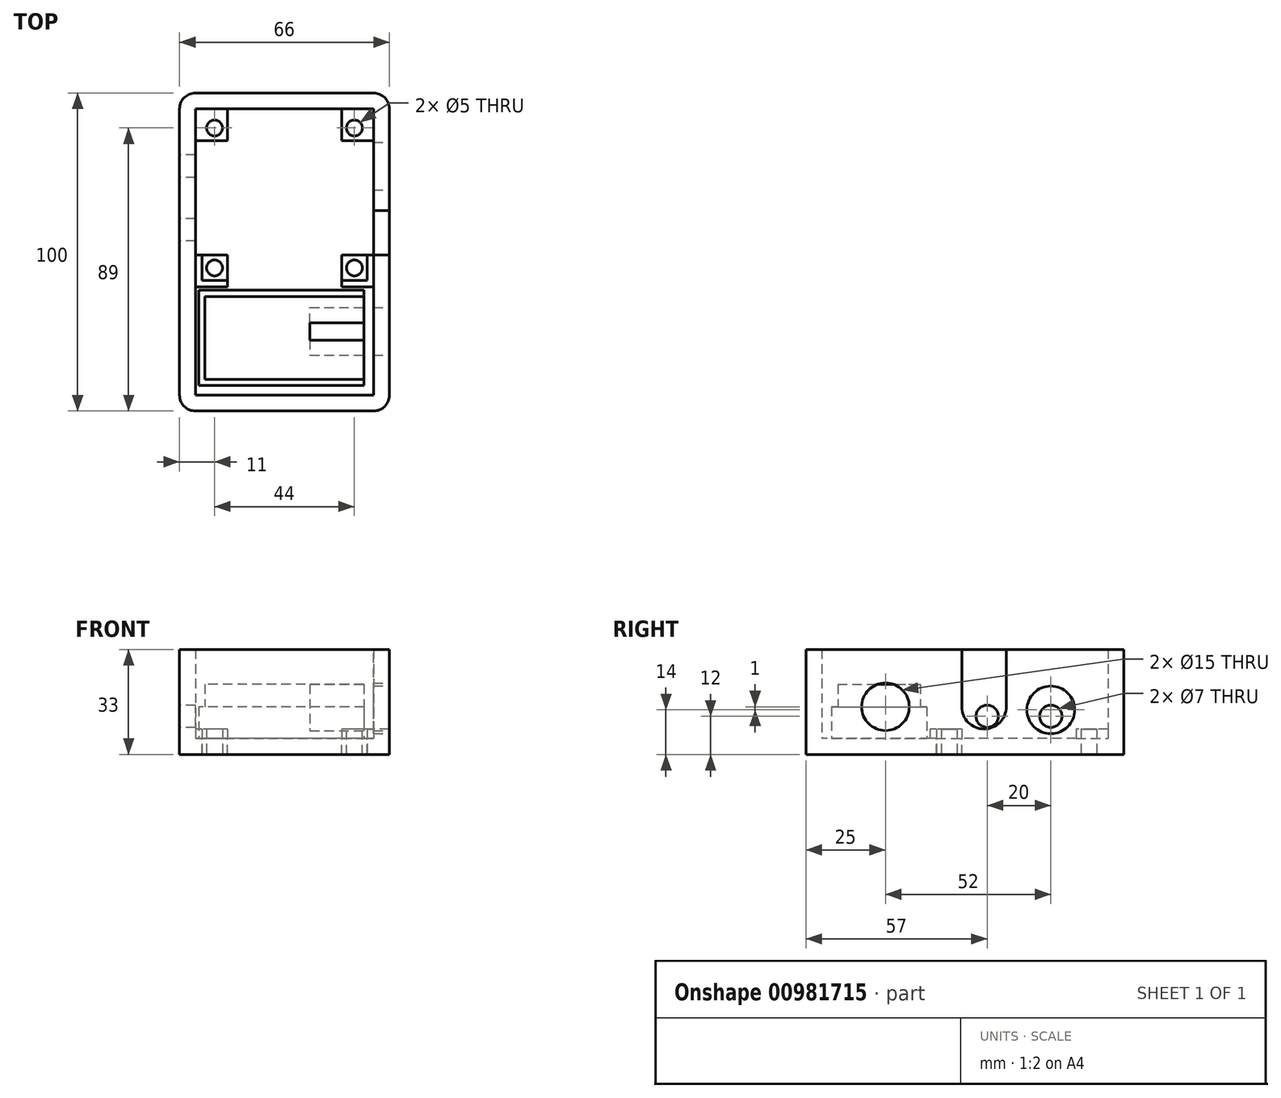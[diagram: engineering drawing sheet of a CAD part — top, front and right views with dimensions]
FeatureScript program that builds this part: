
annotation { "Feature Type Name" : "Feature", "Feature Type Description" : "" }
export const myFeature = defineFeature(function(context is Context, id is Id, definition is map)
    precondition{}
    {
        {
            var Q0;
            Q0=qCreatedBy(makeId("Top.planeOp"),FACE);
            var sketch = newSketch(context, id + "F0", { "sketchPlane" : qUnion([Q0])});
            skLineSegment(sketch, "E0.bottom", {"start": v(26, 26) * mm, "end": v(-26, 26) * mm});
            skLineSegment(sketch, "E0.top", {"start": v(26, -26) * mm, "end": v(-26, -26) * mm});
            skLineSegment(sketch, "E0.left", {"start": v(26, 26) * mm, "end": v(26, -26) * mm});
            skLineSegment(sketch, "E0.right", {"start": v(-26, 26) * mm, "end": v(-26, -26) * mm});
            skPoint(sketch, "E0.middle", {"position": v(0, 0) * mm});
            skCircle(sketch, "E1", {"center": v(-22, 22) * mm, "radius": 2.5 * mm});
            skCircle(sketch, "E2", {"center": v(22, 22) * mm, "radius": 2.5 * mm});
            skLineSegment(sketch, "E3", {"start": v(-22, 22) * mm, "end": v(-26, 22) * mm, "construction": true});
            skLineSegment(sketch, "E4", {"start": v(22, 22) * mm, "end": v(26, 22) * mm, "construction": true});
            skLineSegment(sketch, "E5", {"start": v(-22, 22) * mm, "end": v(-22, 26) * mm, "construction": true});
            skLineSegment(sketch, "E6", {"start": v(22, 22) * mm, "end": v(22, 26) * mm, "construction": true});
            skLineSegment(sketch, "E7", {"start": v(-26, 0) * mm, "end": v(26, 0) * mm, "construction": true});
            skCircle(sketch, "E8.MirrorC", {"center": v(-22, -22) * mm, "radius": 2.5 * mm});
            skCircle(sketch, "E9.MirrorC", {"center": v(22, -22) * mm, "radius": 2.5 * mm});
            skLineSegment(sketch, "E10.bottom", {"start": v(26, -4) * mm, "end": v(13, -4) * mm});
            skLineSegment(sketch, "E10.top", {"start": v(26, -18) * mm, "end": v(13, -18) * mm});
            skLineSegment(sketch, "E10.left", {"start": v(26, -4) * mm, "end": v(26, -18) * mm});
            skLineSegment(sketch, "E10.right", {"start": v(13, -4) * mm, "end": v(13, -18) * mm});
            skLineSegment(sketch, "E11.bottom", {"start": v(26, 15) * mm, "end": v(12, 15) * mm});
            skLineSegment(sketch, "E11.top", {"start": v(26, 5) * mm, "end": v(12, 5) * mm});
            skLineSegment(sketch, "E11.left", {"start": v(26, 15) * mm, "end": v(26, 5) * mm});
            skLineSegment(sketch, "E11.right", {"start": v(12, 15) * mm, "end": v(12, 5) * mm});
            skLineSegment(sketch, "E12.bottom", {"start": v(-26, 16) * mm, "end": v(-11, 16) * mm});
            skLineSegment(sketch, "E12.top", {"start": v(-26, 4) * mm, "end": v(-11, 4) * mm});
            skLineSegment(sketch, "E12.left", {"start": v(-26, 16) * mm, "end": v(-26, 4) * mm});
            skLineSegment(sketch, "E12.right", {"start": v(-11, 16) * mm, "end": v(-11, 4) * mm});
            skLineSegment(sketch, "E13.bottom", {"start": v(-26, -4) * mm, "end": v(-11, -4) * mm});
            skLineSegment(sketch, "E13.top", {"start": v(-26, -16) * mm, "end": v(-11, -16) * mm});
            skLineSegment(sketch, "E13.left", {"start": v(-26, -4) * mm, "end": v(-26, -16) * mm});
            skLineSegment(sketch, "E13.right", {"start": v(-11, -4) * mm, "end": v(-11, -16) * mm});
            skLineSegment(sketch, "E14.0", {"start": v(28, 28) * mm, "end": v(-28, 28) * mm});
            skLineSegment(sketch, "E14.1", {"start": v(28, 28) * mm, "end": v(28, -28) * mm});
            skLineSegment(sketch, "E14.2", {"start": v(28, -28) * mm, "end": v(-28, -28) * mm});
            skLineSegment(sketch, "E14.3", {"start": v(-28, 28) * mm, "end": v(-28, -28) * mm});
            skLineSegment(sketch, "E15.0", {"start": v(33, 33) * mm, "end": v(-33, 33) * mm});
            skLineSegment(sketch, "E15.1", {"start": v(33, 33) * mm, "end": v(33, -67) * mm});
            skLineSegment(sketch, "E15.3", {"start": v(-33, 33) * mm, "end": v(-33, -67) * mm});
            skLineSegment(sketch, "E16.bottom", {"start": v(1, 9) * mm, "end": v(-9, 9) * mm});
            skLineSegment(sketch, "E16.top", {"start": v(1, -1) * mm, "end": v(-9, -1) * mm});
            skLineSegment(sketch, "E16.left", {"start": v(1, 9) * mm, "end": v(1, -1) * mm});
            skLineSegment(sketch, "E16.right", {"start": v(-9, 9) * mm, "end": v(-9, -1) * mm});
            skPoint(sketch, "E16.middle", {"position": v(-4, 4) * mm});
            skCircle(sketch, "E17", {"center": v(-4, 4) * mm, "radius": 5 * mm});
            skLineSegment(sketch, "E18.bottom", {"start": v(26, 26) * mm, "end": v(18, 26) * mm});
            skLineSegment(sketch, "E18.top", {"start": v(26, 18) * mm, "end": v(18, 18) * mm});
            skLineSegment(sketch, "E18.left", {"start": v(26, 26) * mm, "end": v(26, 18) * mm});
            skLineSegment(sketch, "E18.right", {"start": v(18, 26) * mm, "end": v(18, 18) * mm});
            skLineSegment(sketch, "E19.bottom", {"start": v(-26, 26) * mm, "end": v(-18, 26) * mm});
            skLineSegment(sketch, "E19.top", {"start": v(-26, 18) * mm, "end": v(-18, 18) * mm});
            skLineSegment(sketch, "E19.left", {"start": v(-26, 26) * mm, "end": v(-26, 18) * mm});
            skLineSegment(sketch, "E19.right", {"start": v(-18, 26) * mm, "end": v(-18, 18) * mm});
            skLineSegment(sketch, "E20.bottom", {"start": v(-26, -26) * mm, "end": v(-18, -26) * mm});
            skLineSegment(sketch, "E20.top", {"start": v(-26, -18) * mm, "end": v(-18, -18) * mm});
            skLineSegment(sketch, "E20.left", {"start": v(-26, -26) * mm, "end": v(-26, -18) * mm});
            skLineSegment(sketch, "E20.right", {"start": v(-18, -26) * mm, "end": v(-18, -18) * mm});
            skLineSegment(sketch, "E21.bottom", {"start": v(26, -26) * mm, "end": v(18, -26) * mm});
            skLineSegment(sketch, "E21.top", {"start": v(26, -18) * mm, "end": v(18, -18) * mm});
            skLineSegment(sketch, "E21.left", {"start": v(26, -26) * mm, "end": v(26, -18) * mm});
            skLineSegment(sketch, "E21.right", {"start": v(18, -26) * mm, "end": v(18, -18) * mm});
            skLineSegment(sketch, "E22", {"start": v(-18, 26) * mm, "end": v(-18, 28) * mm});
            skLineSegment(sketch, "E23", {"start": v(-26, 18) * mm, "end": v(-28, 18) * mm});
            skLineSegment(sketch, "E24", {"start": v(-18, -26) * mm, "end": v(-18, -28) * mm});
            skLineSegment(sketch, "E25", {"start": v(-26, -18) * mm, "end": v(-28, -18) * mm});
            skLineSegment(sketch, "E26", {"start": v(26, -18) * mm, "end": v(28, -18) * mm});
            skLineSegment(sketch, "E27", {"start": v(18, -26) * mm, "end": v(18, -28) * mm});
            skLineSegment(sketch, "E28", {"start": v(26, 18) * mm, "end": v(28, 18) * mm});
            skLineSegment(sketch, "E29", {"start": v(18, 26) * mm, "end": v(18, 28) * mm});
            skLineSegment(sketch, "E30.bottom", {"start": v(25, -57) * mm, "end": v(-25, -57) * mm});
            skLineSegment(sketch, "E30.top", {"start": v(25, -31) * mm, "end": v(-25, -31) * mm});
            skLineSegment(sketch, "E30.left", {"start": v(25, -57) * mm, "end": v(25, -31) * mm});
            skLineSegment(sketch, "E30.right", {"start": v(-25, -57) * mm, "end": v(-25, -31) * mm});
            skPoint(sketch, "E30.middle", {"position": v(0, -44) * mm});
            skLineSegment(sketch, "E31", {"start": v(-34.4, -67) * mm, "end": v(33, -67) * mm});
            skLineSegment(sketch, "E32", {"start": v(-28, -28) * mm, "end": v(-28, -62) * mm});
            skLineSegment(sketch, "E33", {"start": v(-28, -62) * mm, "end": v(28, -62) * mm});
            skLineSegment(sketch, "E34", {"start": v(28, -62) * mm, "end": v(28, -28) * mm});
            skLineSegment(sketch, "E35.0", {"start": v(25, -59) * mm, "end": v(-27, -59) * mm});
            skLineSegment(sketch, "E35.1", {"start": v(-27, -59) * mm, "end": v(-27, -29) * mm});
            skLineSegment(sketch, "E35.2", {"start": v(25, -29) * mm, "end": v(-27, -29) * mm});
            skLineSegment(sketch, "E36", {"start": v(25, -29) * mm, "end": v(25, -59) * mm});
            skSolve(sketch);
        }
        {
            var Q0;
            Q0=makeQuery(id+"F0.imprint","IMPRINT",FACE,{"disambiguationData":[TD([[makeQuery(id+"F0.imprint","IMPRINT",EDGE,{"derivedFrom":sQuery(id+"F0.wireOp",EDGE,"E1")}),1.0]])]});
            var Q1;
            {var subQ0=sQuery(id+"F0.wireOp",EDGE,"E17");var subQ1=sQuery(id+"F0.wireOp",EDGE,"E16.top");var subQ2=makeQuery(id+"F0.imprint","INTERSECT",VERTEX,{"derivedFrom":[subQ1,subQ0]});Q1=makeQuery(id+"F0.imprint","IMPRINT",FACE,{"disambiguationData":[TD([[makeQuery(id+"F0.imprint","IMPRINT",EDGE,{"disambiguationData":[TD([[subQ2,-1.0]])],"derivedFrom":subQ1}),-1.0]])]});}
            var Q2;
            {var subQ0=sQuery(id+"F0.wireOp",EDGE,"E16.left");var subQ1=sQuery(id+"F0.wireOp",EDGE,"E16.bottom");var subQ2=makeQuery(id+"F0.imprint","INTERSECT",VERTEX,{"derivedFrom":[subQ1,subQ0]});Q2=makeQuery(id+"F0.imprint","IMPRINT",FACE,{"disambiguationData":[TD([[makeQuery(id+"F0.imprint","IMPRINT",EDGE,{"disambiguationData":[TD([[subQ2,-1.0]])],"derivedFrom":subQ1}),1.0]])]});}
            var Q3;
            {var subQ0=sQuery(id+"F0.wireOp",EDGE,"E16.right");var subQ1=sQuery(id+"F0.wireOp",EDGE,"E16.bottom");var subQ2=makeQuery(id+"F0.imprint","INTERSECT",VERTEX,{"derivedFrom":[subQ1,subQ0]});Q3=makeQuery(id+"F0.imprint","IMPRINT",FACE,{"disambiguationData":[TD([[makeQuery(id+"F0.imprint","IMPRINT",EDGE,{"disambiguationData":[TD([[subQ2,1.0]])],"derivedFrom":subQ1}),1.0]])]});}
            var Q4;
            Q4=makeQuery(id+"F0.imprint","IMPRINT",FACE,{"disambiguationData":[TD([[makeQuery(id+"F0.imprint","IMPRINT",EDGE,{"derivedFrom":sQuery(id+"F0.wireOp",EDGE,"E8.MirrorC")}),-1.0]])]});
            var Q5;
            {var subQ0=sQuery(id+"F0.wireOp",EDGE,"E11.bottom");Q5=makeQuery(id+"F0.imprint","IMPRINT",FACE,{"disambiguationData":[TD([[makeQuery(id+"F0.imprint","IMPRINT",EDGE,{"derivedFrom":subQ0}),1.0]])]});}
            var Q6;
            Q6=makeQuery(id+"F0.imprint","IMPRINT",FACE,{"disambiguationData":[TD([[makeQuery(id+"F0.imprint","IMPRINT",EDGE,{"derivedFrom":sQuery(id+"F0.wireOp",EDGE,"E2")}),1.0]])]});
            var Q7;
            {var subQ5=sQuery(id+"F0.wireOp",EDGE,"E10.bottom");Q7=makeQuery(id+"F0.imprint","IMPRINT",FACE,{"disambiguationData":[TD([[makeQuery(id+"F0.imprint","IMPRINT",EDGE,{"derivedFrom":subQ5}),1.0]])]});}
            var Q8;
            {var subQ2=sQuery(id+"F0.wireOp",EDGE,"E22");Q8=makeQuery(id+"F0.imprint","IMPRINT",FACE,{"disambiguationData":[TD([[makeQuery(id+"F0.imprint","IMPRINT",EDGE,{"derivedFrom":subQ2}),-1.0]])]});}
            var Q9;
            {var subQ0=sQuery(id+"F0.wireOp",EDGE,"E17");var subQ1=makeQuery(id+"F0.imprint","INTERSECT",VERTEX,{"derivedFrom":[sQuery(id+"F0.wireOp",EDGE,"E16.left"),subQ0]});Q9=makeQuery(id+"F0.imprint","IMPRINT",FACE,{"disambiguationData":[TD([[makeQuery(id+"F0.imprint","IMPRINT",EDGE,{"disambiguationData":[TD([[subQ1,-1.0]])],"derivedFrom":subQ0}),1.0]])]});}
            var Q10;
            Q10=makeQuery(id+"F0.imprint","IMPRINT",FACE,{"disambiguationData":[TD([[makeQuery(id+"F0.imprint","IMPRINT",EDGE,{"derivedFrom":sQuery(id+"F0.wireOp",EDGE,"E15.0")}),1.0]])]});
            var Q11;
            {var subQ0=sQuery(id+"F0.wireOp",EDGE,"E13.bottom");Q11=makeQuery(id+"F0.imprint","IMPRINT",FACE,{"disambiguationData":[TD([[makeQuery(id+"F0.imprint","IMPRINT",EDGE,{"derivedFrom":subQ0}),-1.0]])]});}
            var Q12;
            Q12=makeQuery(id+"F0.imprint","IMPRINT",FACE,{"disambiguationData":[TD([[makeQuery(id+"F0.imprint","IMPRINT",EDGE,{"derivedFrom":sQuery(id+"F0.wireOp",EDGE,"E9.MirrorC")}),-1.0]])]});
            var Q13;
            {var subQ19=sQuery(id+"F0.wireOp",EDGE,"E10.bottom");Q13=makeQuery(id+"F0.imprint","IMPRINT",FACE,{"disambiguationData":[TD([[makeQuery(id+"F0.imprint","IMPRINT",EDGE,{"derivedFrom":subQ19}),-1.0]])]});}
            var Q14;
            {var subQ0=sQuery(id+"F0.wireOp",EDGE,"E12.bottom");Q14=makeQuery(id+"F0.imprint","IMPRINT",FACE,{"disambiguationData":[TD([[makeQuery(id+"F0.imprint","IMPRINT",EDGE,{"derivedFrom":subQ0}),-1.0]])]});}
            var Q15;
            {var subQ0=sQuery(id+"F0.wireOp",EDGE,"E17");var subQ1=sQuery(id+"F0.wireOp",EDGE,"E16.top");var subQ2=makeQuery(id+"F0.imprint","INTERSECT",VERTEX,{"derivedFrom":[subQ1,subQ0]});Q15=makeQuery(id+"F0.imprint","IMPRINT",FACE,{"disambiguationData":[TD([[makeQuery(id+"F0.imprint","IMPRINT",EDGE,{"disambiguationData":[TD([[subQ2,1.0]])],"derivedFrom":subQ1}),-1.0]])]});}
            var Q16;
            Q16=makeQuery(id+"F0.imprint","IMPRINT",FACE,{"disambiguationData":[TD([[makeQuery(id+"F0.imprint","IMPRINT",EDGE,{"derivedFrom":sQuery(id+"F0.wireOp",EDGE,"E1")}),-1.0]])]});
            var Q17;
            Q17=makeQuery(id+"F0.imprint","IMPRINT",FACE,{"disambiguationData":[TD([[makeQuery(id+"F0.imprint","IMPRINT",EDGE,{"derivedFrom":sQuery(id+"F0.wireOp",EDGE,"E2")}),-1.0]])]});
            var Q18;
            Q18=makeQuery(id+"F0.imprint","IMPRINT",FACE,{"disambiguationData":[TD([[makeQuery(id+"F0.imprint","IMPRINT",EDGE,{"derivedFrom":sQuery(id+"F0.wireOp",EDGE,"E9.MirrorC")}),1.0]])]});
            var Q19;
            Q19=makeQuery(id+"F0.imprint","IMPRINT",FACE,{"disambiguationData":[TD([[makeQuery(id+"F0.imprint","IMPRINT",EDGE,{"derivedFrom":sQuery(id+"F0.wireOp",EDGE,"E8.MirrorC")}),1.0]])]});
            var Q20;
            {var subQ0=sQuery(id+"F0.wireOp",EDGE,"E22");Q20=makeQuery(id+"F0.imprint","IMPRINT",FACE,{"disambiguationData":[TD([[makeQuery(id+"F0.imprint","IMPRINT",EDGE,{"derivedFrom":subQ0}),1.0]])]});}
            var Q21;
            {var subQ0=sQuery(id+"F0.wireOp",EDGE,"E28");Q21=makeQuery(id+"F0.imprint","IMPRINT",FACE,{"disambiguationData":[TD([[makeQuery(id+"F0.imprint","IMPRINT",EDGE,{"derivedFrom":subQ0}),1.0]])]});}
            var Q22;
            {var subQ3=sQuery(id+"F0.wireOp",EDGE,"E26");Q22=makeQuery(id+"F0.imprint","IMPRINT",FACE,{"disambiguationData":[TD([[makeQuery(id+"F0.imprint","IMPRINT",EDGE,{"derivedFrom":subQ3}),1.0]])]});}
            var Q23;
            {var subQ2=sQuery(id+"F0.wireOp",EDGE,"E24");Q23=makeQuery(id+"F0.imprint","IMPRINT",FACE,{"disambiguationData":[TD([[makeQuery(id+"F0.imprint","IMPRINT",EDGE,{"derivedFrom":subQ2}),1.0]])]});}
            var Q24;
            {var subQ4=sQuery(id+"F0.wireOp",EDGE,"E26");Q24=makeQuery(id+"F0.imprint","IMPRINT",FACE,{"disambiguationData":[TD([[makeQuery(id+"F0.imprint","IMPRINT",EDGE,{"derivedFrom":subQ4}),-1.0]])]});}
            var Q25;
            {var subQ4=sQuery(id+"F0.wireOp",EDGE,"E24");Q25=makeQuery(id+"F0.imprint","IMPRINT",FACE,{"disambiguationData":[TD([[makeQuery(id+"F0.imprint","IMPRINT",EDGE,{"derivedFrom":subQ4}),-1.0]])]});}
            var Q26;
            {var subQ3=sQuery(id+"F0.wireOp",EDGE,"E23");Q26=makeQuery(id+"F0.imprint","IMPRINT",FACE,{"disambiguationData":[TD([[makeQuery(id+"F0.imprint","IMPRINT",EDGE,{"derivedFrom":subQ3}),1.0]])]});}
            var Q27;
            Q27=makeQuery(id+"F0.imprint","IMPRINT",FACE,{"disambiguationData":[TD([[makeQuery(id+"F0.imprint","IMPRINT",EDGE,{"derivedFrom":sQuery(id+"F0.wireOp",EDGE,"E30.bottom")}),-1.0]])]});
            var Q28;
            {var subQ5=sQuery(id+"F0.wireOp",EDGE,"E30.bottom");Q28=makeQuery(id+"F0.imprint","IMPRINT",FACE,{"disambiguationData":[TD([[makeQuery(id+"F0.imprint","IMPRINT",EDGE,{"derivedFrom":subQ5}),1.0]])]});}
            var Q29;
            {var subQ8=sQuery(id+"F0.wireOp",EDGE,"E30.left");Q29=makeQuery(id+"F0.imprint","IMPRINT",FACE,{"disambiguationData":[TD([[makeQuery(id+"F0.imprint","IMPRINT",EDGE,{"derivedFrom":subQ8}),-1.0]])]});}
            extrude(context, id + "F1", {"entities" : qUnion([Q0, Q1, Q2, Q3, Q4, Q5, Q6, Q7, Q8, Q9, Q10, Q11, Q12, Q13, Q14, Q15, Q16, Q17, Q18, Q19, Q20, Q21, Q22, Q23, Q24, Q25, Q26, Q27, Q28, Q29]), "oppositeDirection" : true, "depth" : 5 * mm, "offsetDistance" : 25 * mm});
        }
        {
            var Q0;
            Q0=makeQuery(id+"F0.imprint","IMPRINT",FACE,{"disambiguationData":[TD([[makeQuery(id+"F0.imprint","IMPRINT",EDGE,{"derivedFrom":sQuery(id+"F0.wireOp",EDGE,"E15.0")}),1.0]])]});
            extrude(context, id + "F2", {"entities" : qUnion([Q0]), "operationType" : NewBodyOperationType.ADD, "depth" : 28 * mm, "offsetDistance" : 25 * mm});
        }
        {
            var Q0;
            Q0=makeQuery(id+"F0.imprint","IMPRINT",FACE,{"disambiguationData":[TD([[makeQuery(id+"F0.imprint","IMPRINT",EDGE,{"derivedFrom":sQuery(id+"F0.wireOp",EDGE,"E1")}),-1.0]])]});
            var Q1;
            {var subQ0=sQuery(id+"F0.wireOp",EDGE,"E22");Q1=makeQuery(id+"F0.imprint","IMPRINT",FACE,{"disambiguationData":[TD([[makeQuery(id+"F0.imprint","IMPRINT",EDGE,{"derivedFrom":subQ0}),1.0]])]});}
            var Q2;
            {var subQ0=sQuery(id+"F0.wireOp",EDGE,"E28");Q2=makeQuery(id+"F0.imprint","IMPRINT",FACE,{"disambiguationData":[TD([[makeQuery(id+"F0.imprint","IMPRINT",EDGE,{"derivedFrom":subQ0}),1.0]])]});}
            var Q3;
            Q3=makeQuery(id+"F0.imprint","IMPRINT",FACE,{"disambiguationData":[TD([[makeQuery(id+"F0.imprint","IMPRINT",EDGE,{"derivedFrom":sQuery(id+"F0.wireOp",EDGE,"E2")}),-1.0]])]});
            var Q4;
            {var subQ4=sQuery(id+"F0.wireOp",EDGE,"E24");Q4=makeQuery(id+"F0.imprint","IMPRINT",FACE,{"disambiguationData":[TD([[makeQuery(id+"F0.imprint","IMPRINT",EDGE,{"derivedFrom":subQ4}),-1.0]])]});}
            var Q5;
            Q5=makeQuery(id+"F0.imprint","IMPRINT",FACE,{"disambiguationData":[TD([[makeQuery(id+"F0.imprint","IMPRINT",EDGE,{"derivedFrom":sQuery(id+"F0.wireOp",EDGE,"E8.MirrorC")}),1.0]])]});
            var Q6;
            {var subQ4=sQuery(id+"F0.wireOp",EDGE,"E26");Q6=makeQuery(id+"F0.imprint","IMPRINT",FACE,{"disambiguationData":[TD([[makeQuery(id+"F0.imprint","IMPRINT",EDGE,{"derivedFrom":subQ4}),-1.0]])]});}
            var Q7;
            Q7=makeQuery(id+"F0.imprint","IMPRINT",FACE,{"disambiguationData":[TD([[makeQuery(id+"F0.imprint","IMPRINT",EDGE,{"derivedFrom":sQuery(id+"F0.wireOp",EDGE,"E9.MirrorC")}),1.0]])]});
            extrude(context, id + "F3", {"entities" : qUnion([Q0, Q1, Q2, Q3, Q4, Q5, Q6, Q7]), "operationType" : NewBodyOperationType.ADD, "depth" : 3 * mm, "offsetDistance" : 25 * mm});
        }
        {
            var Q0;
            Q0=makeQuery(id+"F2.opExtrude","CAP_FACE",FACE,{"disambiguationData":[OSD([sQuery(id+"F0.wireOp",EDGE,"E14.0"),sQuery(id+"F0.wireOp",EDGE,"E14.1"),sQuery(id+"F0.wireOp",EDGE,"E14.3"),sQuery(id+"F0.wireOp",EDGE,"E15.0"),sQuery(id+"F0.wireOp",EDGE,"E15.1"),sQuery(id+"F0.wireOp",EDGE,"E15.3"),sQuery(id+"F0.wireOp",EDGE,"E31"),sQuery(id+"F0.wireOp",EDGE,"E32"),sQuery(id+"F0.wireOp",EDGE,"E33"),sQuery(id+"F0.wireOp",EDGE,"E34")])],"isStart":false});
            var sketch = newSketch(context, id + "F4", { "sketchPlane" : qUnion([Q0])});
            skLineSegment(sketch, "E37.0.0", {"start": v(-11, -4) * mm, "end": v(-26, -4) * mm});
            skLineSegment(sketch, "E37.0.1", {"start": v(-26, -4) * mm, "end": v(-26, -16) * mm});
            skLineSegment(sketch, "E37.0.2", {"start": v(-26, -16) * mm, "end": v(-11, -16) * mm});
            skLineSegment(sketch, "E37.0.3", {"start": v(-11, -16) * mm, "end": v(-11, -4) * mm});
            skLineSegment(sketch, "E38.0.0", {"start": v(13, -18) * mm, "end": v(18, -18) * mm});
            skLineSegment(sketch, "E38.0.1", {"start": v(18, -18) * mm, "end": v(26, -18) * mm});
            skLineSegment(sketch, "E38.0.2", {"start": v(26, -18) * mm, "end": v(26, -4) * mm});
            skLineSegment(sketch, "E38.0.3", {"start": v(26, -4) * mm, "end": v(13, -4) * mm});
            skLineSegment(sketch, "E38.0.4", {"start": v(13, -4) * mm, "end": v(13, -18) * mm});
            skLineSegment(sketch, "E39.0.0", {"start": v(26, 5) * mm, "end": v(26, 15) * mm});
            skLineSegment(sketch, "E39.0.1", {"start": v(26, 15) * mm, "end": v(12, 15) * mm});
            skLineSegment(sketch, "E39.0.2", {"start": v(12, 15) * mm, "end": v(12, 5) * mm});
            skLineSegment(sketch, "E39.0.3", {"start": v(12, 5) * mm, "end": v(26, 5) * mm});
            skLineSegment(sketch, "E40.0.0", {"start": v(-11, 16) * mm, "end": v(-26, 16) * mm});
            skLineSegment(sketch, "E40.0.1", {"start": v(-26, 16) * mm, "end": v(-26, 4) * mm});
            skLineSegment(sketch, "E40.0.2", {"start": v(-26, 4) * mm, "end": v(-11, 4) * mm});
            skLineSegment(sketch, "E40.0.3", {"start": v(-11, 4) * mm, "end": v(-11, 16) * mm});
            skArc(sketch, "E41.0.0", {"start": v(-4, -1) * mm, "mid": v(-0.46, 0.46) * mm, "end": v(1, 4) * mm});
            skArc(sketch, "E41.0.1", {"start": v(1, 4) * mm, "mid": v(-0.46, 7.54) * mm, "end": v(-4, 9) * mm});
            skArc(sketch, "E41.0.2", {"start": v(-4, 9) * mm, "mid": v(-7.54, 7.54) * mm, "end": v(-9, 4) * mm});
            skArc(sketch, "E41.0.3", {"start": v(-9, 4) * mm, "mid": v(-7.54, 0.46) * mm, "end": v(-4, -1) * mm});
            skLineSegment(sketch, "E42.bottom", {"start": v(28, -4) * mm, "end": v(33, -4) * mm});
            skLineSegment(sketch, "E42.top", {"start": v(28, -18) * mm, "end": v(33, -18) * mm});
            skLineSegment(sketch, "E42.left", {"start": v(28, -4) * mm, "end": v(28, -18) * mm});
            skLineSegment(sketch, "E42.right", {"start": v(33, -4) * mm, "end": v(33, -18) * mm});
            skLineSegment(sketch, "E43.bottom", {"start": v(28, 15) * mm, "end": v(33, 15) * mm});
            skLineSegment(sketch, "E43.top", {"start": v(28, 5) * mm, "end": v(33, 5) * mm});
            skLineSegment(sketch, "E43.left", {"start": v(28, 15) * mm, "end": v(28, 5) * mm});
            skLineSegment(sketch, "E43.right", {"start": v(33, 15) * mm, "end": v(33, 5) * mm});
            skLineSegment(sketch, "E44.bottom", {"start": v(-28, 16) * mm, "end": v(-33, 16) * mm});
            skLineSegment(sketch, "E44.top", {"start": v(-28, 4) * mm, "end": v(-33, 4) * mm});
            skLineSegment(sketch, "E44.left", {"start": v(-28, 16) * mm, "end": v(-28, 4) * mm});
            skLineSegment(sketch, "E44.right", {"start": v(-33, 16) * mm, "end": v(-33, 4) * mm});
            skLineSegment(sketch, "E45.bottom", {"start": v(-28, -4) * mm, "end": v(-33, -4) * mm});
            skLineSegment(sketch, "E45.top", {"start": v(-28, -16) * mm, "end": v(-33, -16) * mm});
            skLineSegment(sketch, "E45.left", {"start": v(-28, -4) * mm, "end": v(-28, -16) * mm});
            skLineSegment(sketch, "E45.right", {"start": v(-33, -4) * mm, "end": v(-33, -16) * mm});
            skSolve(sketch);
        }
        {
            var Q0;
            Q0=makeQuery(id+"F0.imprint","IMPRINT",FACE,{"disambiguationData":[TD([[makeQuery(id+"F0.imprint","IMPRINT",EDGE,{"derivedFrom":sQuery(id+"F0.wireOp",EDGE,"E30.bottom")}),-1.0]])]});
            extrude(context, id + "F5", {"entities" : qUnion([Q0]), "depth" : 17 * mm, "offsetDistance" : 25 * mm});
        }
        {
            var Q0;
            {var subQ0=sQuery(id+"F0.wireOp",EDGE,"E15.3");var subQ1=sQuery(id+"F0.wireOp",EDGE,"E15.0");Q0=makeQuery(id+"F2.boolean.opBoolean","MERGE",EDGE,{"derivedFrom":[makeQuery(id+"F1.opExtrude","SWEPT_EDGE",EDGE,{"disambiguationData":[OSD([subQ1,subQ0])]}),makeQuery(id+"F2.opExtrude","SWEPT_EDGE",EDGE,{"disambiguationData":[OSD([subQ1,subQ0])]})]});}
            var Q1;
            {var subQ0=sQuery(id+"F0.wireOp",EDGE,"E31");var subQ1=sQuery(id+"F0.wireOp",EDGE,"E15.3");Q1=makeQuery(id+"F2.boolean.opBoolean","MERGE",EDGE,{"derivedFrom":[makeQuery(id+"F1.opExtrude","SWEPT_EDGE",EDGE,{"disambiguationData":[OSD([subQ1,subQ0])]}),makeQuery(id+"F2.opExtrude","SWEPT_EDGE",EDGE,{"disambiguationData":[OSD([subQ1,subQ0])]})]});}
            var Q2;
            {var subQ0=sQuery(id+"F0.wireOp",EDGE,"E31");var subQ1=sQuery(id+"F0.wireOp",EDGE,"E15.1");Q2=makeQuery(id+"F2.boolean.opBoolean","MERGE",EDGE,{"derivedFrom":[makeQuery(id+"F1.opExtrude","SWEPT_EDGE",EDGE,{"disambiguationData":[OSD([subQ1,subQ0])]}),makeQuery(id+"F2.opExtrude","SWEPT_EDGE",EDGE,{"disambiguationData":[OSD([subQ1,subQ0])]})]});}
            var Q3;
            {var subQ0=sQuery(id+"F0.wireOp",EDGE,"E15.1");var subQ1=sQuery(id+"F0.wireOp",EDGE,"E15.0");Q3=makeQuery(id+"F2.boolean.opBoolean","MERGE",EDGE,{"derivedFrom":[makeQuery(id+"F1.opExtrude","SWEPT_EDGE",EDGE,{"disambiguationData":[OSD([subQ1,subQ0])]}),makeQuery(id+"F2.opExtrude","SWEPT_EDGE",EDGE,{"disambiguationData":[OSD([subQ1,subQ0])]})]});}
            fillet(context, id + "F6", {"entities" : qUnion([Q0, Q1, Q2, Q3]), "radius" : 5 * mm, "tangentPropagation" : true, "allowEdgeOverflow" : false});
        }
        {
            var Q0;
            Q0=makeQuery(id+"F0.imprint","IMPRINT",FACE,{"disambiguationData":[TD([[makeQuery(id+"F0.imprint","IMPRINT",EDGE,{"derivedFrom":sQuery(id+"F0.wireOp",EDGE,"E2")}),1.0]])]});
            var Q1;
            Q1=makeQuery(id+"F0.imprint","IMPRINT",FACE,{"disambiguationData":[TD([[makeQuery(id+"F0.imprint","IMPRINT",EDGE,{"derivedFrom":sQuery(id+"F0.wireOp",EDGE,"E9.MirrorC")}),-1.0]])]});
            var Q2;
            Q2=makeQuery(id+"F0.imprint","IMPRINT",FACE,{"disambiguationData":[TD([[makeQuery(id+"F0.imprint","IMPRINT",EDGE,{"derivedFrom":sQuery(id+"F0.wireOp",EDGE,"E8.MirrorC")}),-1.0]])]});
            var Q3;
            Q3=makeQuery(id+"F0.imprint","IMPRINT",FACE,{"disambiguationData":[TD([[makeQuery(id+"F0.imprint","IMPRINT",EDGE,{"derivedFrom":sQuery(id+"F0.wireOp",EDGE,"E1")}),1.0]])]});
            extrude(context, id + "F7", {"entities" : qUnion([Q0, Q1, Q2, Q3]), "operationType" : NewBodyOperationType.REMOVE, "oppositeDirection" : true, "depth" : 25 * mm, "offsetDistance" : 25 * mm});
        }
        {
            var Q0;
            {var subQ0=sQuery(id+"F0.wireOp",EDGE,"E15.1");Q0=makeQuery(id+"F2.boolean.opBoolean","MERGE",FACE,{"derivedFrom":[makeQuery(id+"F1.opExtrude","SWEPT_FACE",FACE,{"disambiguationData":[OSD([subQ0])]}),makeQuery(id+"F2.opExtrude","SWEPT_FACE",FACE,{"disambiguationData":[OSD([subQ0])]})]});}
            var sketch = newSketch(context, id + "F8", { "sketchPlane" : qUnion([Q0])});
            skCircle(sketch, "E46", {"center": v(-42, 10) * mm, "radius": 7.5 * mm});
            skLineSegment(sketch, "E47.0", {"start": v(15, 0) * mm, "end": v(5, 0) * mm});
            skCircle(sketch, "E48", {"center": v(10, 9) * mm, "radius": 7.5 * mm});
            skPoint(sketch, "E49", {"position": v(2.5, 9) * mm});
            skPoint(sketch, "E50", {"position": v(17.5, 9) * mm});
            skPoint(sketch, "E51", {"position": v(10, 0) * mm});
            skSolve(sketch);
        }
        {
            var Q0;
            Q0=makeQuery(id+"F8.imprint","IMPRINT",FACE,{"disambiguationData":[TD([[makeQuery(id+"F8.imprint","IMPRINT",EDGE,{"derivedFrom":sQuery(id+"F8.wireOp",EDGE,"E46")}),1.0]])]});
            var Q1;
            Q1=makeQuery(id+"F8.imprint","IMPRINT",FACE,{"disambiguationData":[TD([[makeQuery(id+"F8.imprint","IMPRINT",EDGE,{"derivedFrom":sQuery(id+"F8.wireOp",EDGE,"E48")}),1.0]])]});
            extrude(context, id + "F9", {"entities" : qUnion([Q0, Q1]), "operationType" : NewBodyOperationType.REMOVE, "oppositeDirection" : true, "depth" : 25 * mm, "offsetDistance" : 25 * mm});
        }
        {
            var Q0;
            {var subQ5=sQuery(id+"F0.wireOp",EDGE,"E30.bottom");Q0=makeQuery(id+"F0.imprint","IMPRINT",FACE,{"disambiguationData":[TD([[makeQuery(id+"F0.imprint","IMPRINT",EDGE,{"derivedFrom":subQ5}),1.0]])]});}
            extrude(context, id + "F10", {"entities" : qUnion([Q0]), "operationType" : NewBodyOperationType.ADD, "depth" : 10 * mm, "offsetDistance" : 25 * mm});
        }
        {
            var Q0;
            Q0=makeQuery(id+"F4.imprint","IMPRINT",FACE,{"disambiguationData":[TD([[makeQuery(id+"F4.imprint","IMPRINT",EDGE,{"derivedFrom":sQuery(id+"F4.wireOp",EDGE,"E42.bottom")}),-1.0]])]});
            extrude(context, id + "F11", {"entities" : qUnion([Q0]), "operationType" : NewBodyOperationType.REMOVE, "oppositeDirection" : true, "depth" : 25 * mm, "offsetDistance" : 25 * mm});
        }
        {
            var Q0;
            Q0=makeQuery(id+"F11.boolean.opBoolean","COPY",EDGE,{"derivedFrom":makeQuery(id+"F11.opExtrude","CAP_EDGE",EDGE,{"disambiguationData":[OSD([sQuery(id+"F4.wireOp",EDGE,"E42.bottom")])],"isStart":false})});
            var Q1;
            Q1=makeQuery(id+"F11.boolean.opBoolean","COPY",EDGE,{"derivedFrom":makeQuery(id+"F11.opExtrude","CAP_EDGE",EDGE,{"disambiguationData":[OSD([sQuery(id+"F4.wireOp",EDGE,"E42.top")])],"isStart":false})});
            fillet(context, id + "F12", {"entities" : qUnion([Q0, Q1]), "radius" : 7 * mm, "tangentPropagation" : true, "allowEdgeOverflow" : false});
        }
        {
            var Q0;
            {var subQ0=sQuery(id+"F0.wireOp",EDGE,"E15.3");Q0=makeQuery(id+"F2.boolean.opBoolean","MERGE",FACE,{"derivedFrom":[makeQuery(id+"F1.opExtrude","SWEPT_FACE",FACE,{"disambiguationData":[OSD([subQ0])]}),makeQuery(id+"F2.opExtrude","SWEPT_FACE",FACE,{"disambiguationData":[OSD([subQ0])]})]});}
            var sketch = newSketch(context, id + "F13", { "sketchPlane" : qUnion([Q0])});
            skLineSegment(sketch, "E52.0", {"start": v(-16, 0) * mm, "end": v(-4, 0) * mm});
            skLineSegment(sketch, "E53.0", {"start": v(4, 0) * mm, "end": v(16, 0) * mm});
            skCircle(sketch, "E54", {"center": v(-10, 7) * mm, "radius": 3.5 * mm});
            skCircle(sketch, "E55", {"center": v(10, 7) * mm, "radius": 3.5 * mm});
            skPoint(sketch, "E56", {"position": v(-10, 0) * mm});
            skPoint(sketch, "E57", {"position": v(10, 0) * mm});
            skSolve(sketch);
        }
        {
            var Q0;
            Q0=makeQuery(id+"F13.imprint","IMPRINT",FACE,{"disambiguationData":[TD([[makeQuery(id+"F13.imprint","IMPRINT",EDGE,{"derivedFrom":sQuery(id+"F13.wireOp",EDGE,"E54")}),1.0]])]});
            var Q1;
            Q1=makeQuery(id+"F13.imprint","IMPRINT",FACE,{"disambiguationData":[TD([[makeQuery(id+"F13.imprint","IMPRINT",EDGE,{"derivedFrom":sQuery(id+"F13.wireOp",EDGE,"E55")}),1.0]])]});
            extrude(context, id + "F14", {"entities" : qUnion([Q0, Q1]), "operationType" : NewBodyOperationType.REMOVE, "oppositeDirection" : true, "depth" : 25 * mm, "offsetDistance" : 25 * mm});
        }
    });
